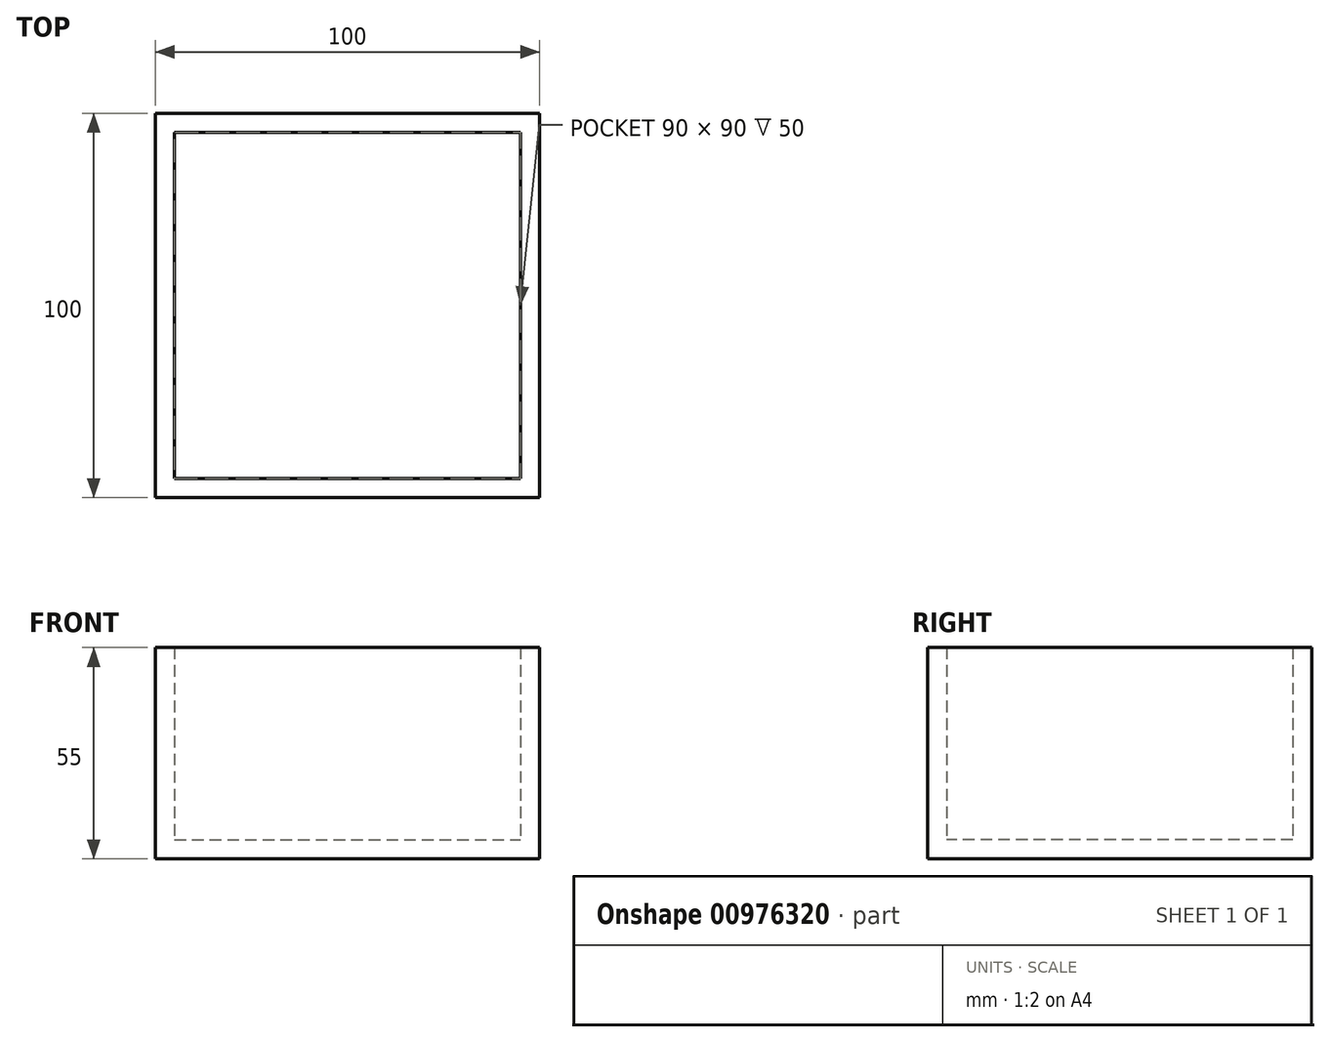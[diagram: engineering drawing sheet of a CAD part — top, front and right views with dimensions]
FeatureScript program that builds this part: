
annotation { "Feature Type Name" : "Feature", "Feature Type Description" : "" }
export const myFeature = defineFeature(function(context is Context, id is Id, definition is map)
    precondition{}
    {
        {
            var Q0;
            Q0=qCreatedBy(makeId("Top.planeOp"),FACE);
            var sketch = newSketch(context, id + "F0", { "sketchPlane" : qUnion([Q0])});
            skLineSegment(sketch, "E0.bottom", {"start": v(-50, 50.52) * mm, "end": v(50, 50.52) * mm});
            skLineSegment(sketch, "E0.top", {"start": v(-50, -49.48) * mm, "end": v(50, -49.48) * mm});
            skLineSegment(sketch, "E0.left", {"start": v(-50, 50.52) * mm, "end": v(-50, -49.48) * mm});
            skLineSegment(sketch, "E0.right", {"start": v(50, 50.52) * mm, "end": v(50, -49.48) * mm});
            skSolve(sketch);
        }
        {
            var Q0;
            Q0=makeQuery(id+"F0.imprint","IMPRINT",FACE,{"disambiguationData":[TD([[makeQuery(id+"F0.imprint","IMPRINT",EDGE,{"derivedFrom":sQuery(id+"F0.wireOp",EDGE,"E0.bottom")}),-1.0]])]});
            extrude(context, id + "F1", {"entities" : qUnion([Q0]), "oppositeDirection" : true, "depth" : 5 * mm, "offsetDistance" : 25 * mm});
        }
        {
            var Q0;
            Q0=makeQuery(id+"F1.opExtrude","CAP_FACE",FACE,{"disambiguationData":[OSD([sQuery(id+"F0.wireOp",EDGE,"E0.bottom"),sQuery(id+"F0.wireOp",EDGE,"E0.top"),sQuery(id+"F0.wireOp",EDGE,"E0.left"),sQuery(id+"F0.wireOp",EDGE,"E0.right")])],"isStart":true});
            var sketch = newSketch(context, id + "F2", { "sketchPlane" : qUnion([Q0])});
            skLineSegment(sketch, "E1.0", {"start": v(-45, 45.52) * mm, "end": v(45, 45.52) * mm});
            skLineSegment(sketch, "E1.1", {"start": v(-45, 45.52) * mm, "end": v(-45, -44.48) * mm});
            skLineSegment(sketch, "E1.2", {"start": v(-45, -44.48) * mm, "end": v(45, -44.48) * mm});
            skLineSegment(sketch, "E1.3", {"start": v(45, 45.52) * mm, "end": v(45, -44.48) * mm});
            skSolve(sketch);
        }
        {
            var Q0;
            Q0=makeQuery(id+"F2.imprint","IMPRINT",FACE,{"disambiguationData":[TD([[makeQuery(id+"F2.imprint","IMPRINT",EDGE,{"derivedFrom":sQuery(id+"F2.wireOp",EDGE,"E1.0")}),1.0]])]});
            extrude(context, id + "F3", {"entities" : qUnion([Q0]), "operationType" : NewBodyOperationType.ADD, "depth" : 50 * mm, "offsetDistance" : 25 * mm});
        }
    });
